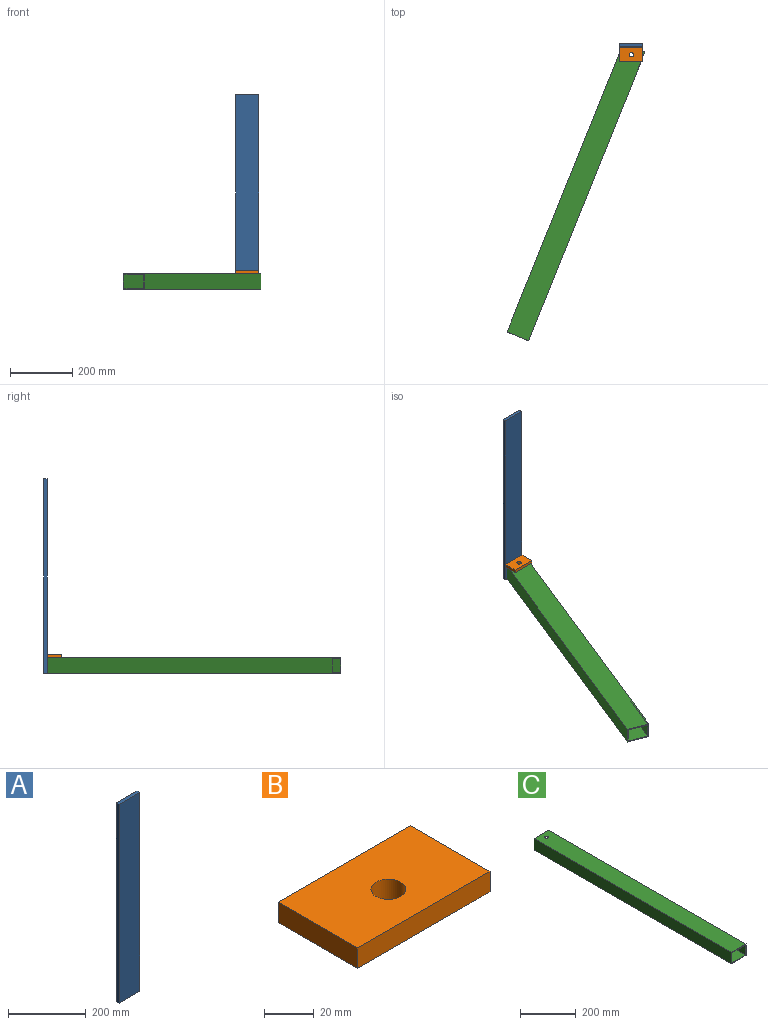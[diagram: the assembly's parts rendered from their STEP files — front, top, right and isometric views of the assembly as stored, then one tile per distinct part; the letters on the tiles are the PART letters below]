
ASSEMBLY  parts=3 mates=2
PART A: 6 faces, bbox 75x10x625 mm
  f0: plane 625x10mm, normal (1,0,0), area 6250mm2, adj f1,f3,f4,f5
  f1: plane 625x75mm, normal (0,1,0), area 46875mm2, adj f0,f2,f4,f5
  f2: plane 625x10mm, normal (-1,0,0), area 6250mm2, adj f1,f3,f4,f5
  f3: plane 625x75mm, normal (0,-1,0), area 46875mm2, adj f0,f2,f4,f5
  f4: plane 75x10mm, normal (0,0,1), area 750mm2, adj f0,f1,f2,f3
  f5: plane 75x10mm, normal (0,0,-1), area 750mm2, adj f0,f1,f2,f3
PART B: 7 faces, bbox 75x45x10 mm
  f0: plane 75x10mm, normal (0,-1,0), area 750mm2, adj f1,f3,f5,f6
  f1: plane 45x10mm, normal (1,0,0), area 450mm2, adj f0,f2,f5,f6
  f2: plane 75x10mm, normal (0,1,0), area 750mm2, adj f1,f3,f5,f6
  f3: plane 45x10mm, normal (-1,0,0), area 450mm2, adj f0,f2,f5,f6
  f4: cylinder r=7mm len=14mm, axis (0,0,-1), area 439.8mm2, adj f5,f6
  f5: plane 75x45mm, normal (0,0,1), area 3221.1mm2, adj f0,f1,f2,f3,f4
  f6: plane 75x45mm, normal (0,0,-1), area 3221.1mm2, adj f0,f1,f2,f3,f4
PART C: 12 faces, bbox 75x1000x50 mm
  f0: plane 1000x75mm, normal (0,0,-1), area 74846.1mm2, adj f1,f7,f8,f9,f11
  f1: plane 1000x50mm, normal (1,0,0), area 50000mm2, adj f0,f2,f8,f9
  f2: plane 1000x75mm, normal (0,0,1), area 74846.1mm2, adj f1,f7,f8,f9,f10
  f3: plane 1000x69mm, normal (0,0,1), area 68846.1mm2, adj f4,f6,f8,f9,f11
  f4: plane 1000x44mm, normal (1,0,0), area 44000mm2, adj f3,f5,f8,f9
  f5: plane 1000x69mm, normal (0,0,-1), area 68846.1mm2, adj f4,f6,f8,f9,f10
  f6: plane 1000x44mm, normal (-1,0,0), area 44000mm2, adj f3,f5,f8,f9
  f7: plane 1000x50mm, normal (-1,0,0), area 50000mm2, adj f0,f2,f8,f9
  f8: plane 75x50mm, normal (0,-1,0), area 714mm2, adj f0,f1,f2,f3,f4,f5,f6,f7
  f9: plane 75x50mm, normal (0,1,0), area 714mm2, adj f0,f1,f2,f3,f4,f5,f6,f7
  f10: cylinder r=7mm len=14mm, axis (0,0,1), area 131.9mm2, adj f2,f5
  f11: cylinder r=7mm len=14mm, axis (0,0,1), area 131.9mm2, adj f0,f3
PLACE A t=(-199.2,362.97,-309.28)mm fixed
PLACE B t=(-199.2,367.97,-309.28)mm
PLACE C rot(axis=(0,0,-1),21.9deg) t=(-189.86,366.16,-309.28)mm
MATE revolute B.f4 <-> C.f10  axis (0,0,-1) through (-199.2,342.97,-284.28)mm
MATE fastened A.f3 <-> B.f2  axis (0,-1,0) through (-199.2,367.97,-21.78)mm
